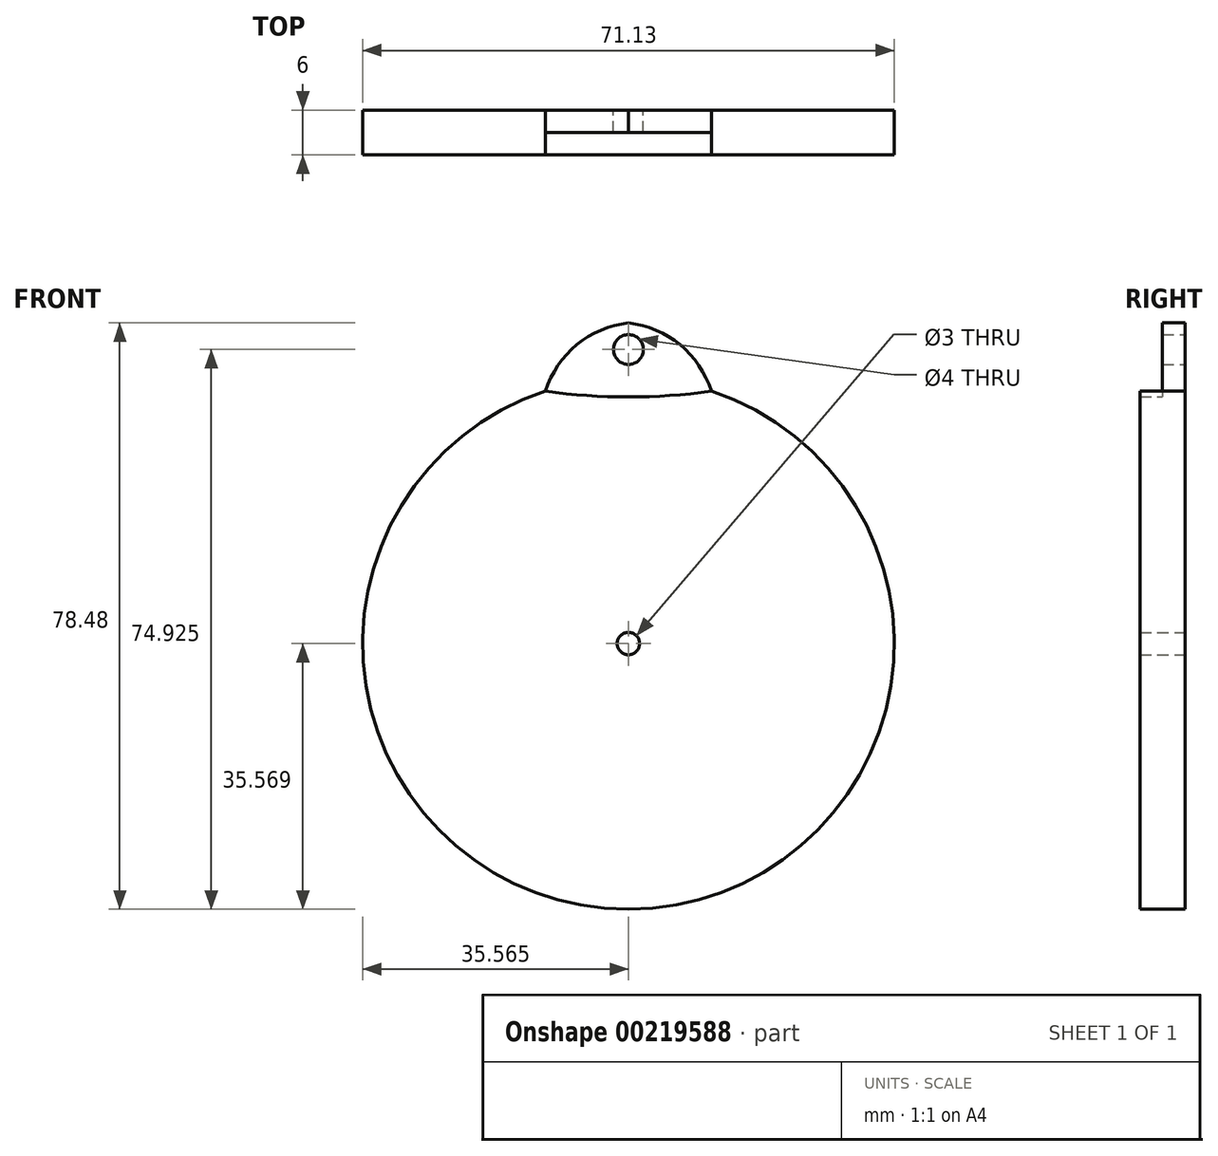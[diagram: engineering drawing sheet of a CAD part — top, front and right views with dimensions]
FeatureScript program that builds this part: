
annotation { "Feature Type Name" : "Feature", "Feature Type Description" : "" }
export const myFeature = defineFeature(function(context is Context, id is Id, definition is map)
    precondition{}
    {
        {
            var Q0;
            Q0=qCreatedBy(makeId("Front.planeOp"),FACE);
            var sketch = newSketch(context, id + "F0", { "sketchPlane" : qUnion([Q0])});
            skArc(sketch, "E0", {"start": v(-47.35, 43.66) * mm, "mid": v(-36.25, -25.7) * mm, "end": v(-25.16, 43.66) * mm});
            skCircle(sketch, "E1", {"center": v(-36.25, 49.22) * mm, "radius": 2 * mm});
            skArc(sketch, "E2", {"start": v(-47.35, 43.66) * mm, "mid": v(-36.25, 42.88) * mm, "end": v(-25.16, 43.66) * mm});
            skCircle(sketch, "E3", {"center": v(-36.25, 9.87) * mm, "radius": 1.5 * mm});
            skLineSegment(sketch, "E4", {"start": v(-36.25, 9.87) * mm, "end": v(-36.25, 57.2) * mm});
            skArc(sketch, "E5", {"start": v(-36.25, 52.78) * mm, "mid": v(-43.15, 49.86) * mm, "end": v(-47.35, 43.66) * mm});
            skPoint(sketch, "E5.startSnap0", {"position": v(-35.64, 52.87) * mm});
            skArc(sketch, "E6.MirrorCS", {"start": v(-36.25, 52.78) * mm, "mid": v(-29.36, 49.86) * mm, "end": v(-25.16, 43.66) * mm});
            skPoint(sketch, "E7.orphan", {"position": v(-37.64, 52.87) * mm});
            skPoint(sketch, "E8.orphan", {"position": v(-34.87, 52.87) * mm});
            skSolve(sketch);
        }
        {
            var Q0;
            Q0 = qSketchRegion(id + "F0", true);
            extrude(context, id + "F1", {"entities" : qUnion([Q0]), "depth" : 3 * mm});
        }
        {
            var Q0;
            Q0=makeQuery(id+"F0.imprint","IMPRINT",FACE,{"disambiguationData":[TD([[makeQuery(id+"F0.imprint","IMPRINT",EDGE,{"derivedFrom":sQuery(id+"F0.wireOp",EDGE,"E0")}),1.0]])]});
            extrude(context, id + "F2", {"entities" : qUnion([Q0]), "operationType" : NewBodyOperationType.ADD, "depth" : 6 * mm});
        }
        {
            var Q0;
            Q0=qCreatedBy(makeId("Top.planeOp"),FACE);
            var sketch = newSketch(context, id + "F3", { "sketchPlane" : qUnion([Q0])});
            skCircle(sketch, "E9", {"center": v(31.44, -8.45) * mm, "radius": 2 * mm});
            skSolve(sketch);
        }
        {
            var Q0;
            Q0=sQuery(id+"F3.wireOp",EDGE,"E9");
            extrude(context, id + "F4", {"bodyType" : ToolBodyType.SURFACE, "surfaceEntities" : qUnion([Q0]), "depth" : 10 * mm});
        }
    });
